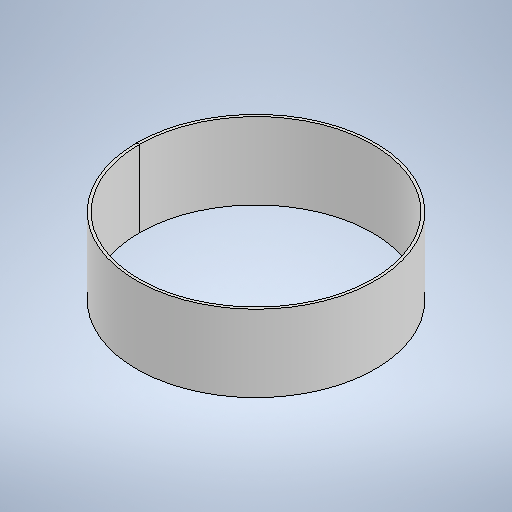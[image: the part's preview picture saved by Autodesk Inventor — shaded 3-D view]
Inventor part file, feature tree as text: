
AUTODESK INVENTOR PART (.ipt)
format: ipt  version: 2025.1 (Build 291241020, 241B)  size: 276,480 bytes
history: native  units: mm
features: sketch x2, revolve x1, extrude x1, other x1
ambient origin geometry x8: Origin, YZ Plane, XZ Plane, XY Plane, X Axis, Y Axis, Z Axis, Center Point
bodies: Solid1 (feature_tree)
feature tree (5):
  revolve  "Revolution1"  [1 undecoded]
  extrude  "Extrusion1"  Depth=6.0mm
  sketch  "Sketch1"  dims[d1=6.0mm d3=6.0mm d5=120.0mm]
  sketch  "Sketch2"  dims[d6=62.8144mm d7=6.0mm d8=50.0mm d9=1212.0mm d10=0.0mm d11=0.0mm d12=530.0mm]
  other  "Definition1"
note: 1 required parameter value undecoded (feature->parameter linkage not recoverable at this tier; creation-order binding heuristic only, values carry confidence <= 0.55)
